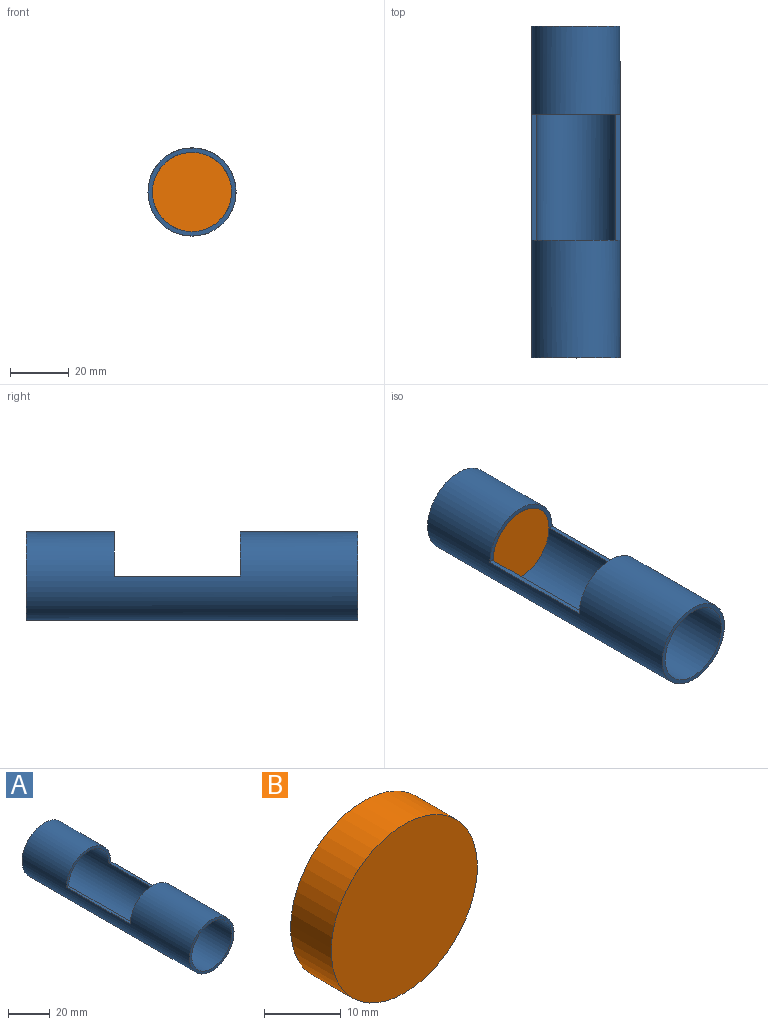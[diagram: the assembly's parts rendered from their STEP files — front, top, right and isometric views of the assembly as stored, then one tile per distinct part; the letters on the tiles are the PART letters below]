
ASSEMBLY  parts=2 mates=1
PART A: 8 faces, bbox 30x113x30 mm
  f0: plane 30x15mm, normal (0,1,0), area 67.2mm2, adj f1,f2,f4,f5
  f1: cylinder r=13.5mm len=113mm, axis (0,1,0), area 7761.3mm2, adj f0,f3,f4,f5,f6,f7
  f2: cylinder r=15mm len=113mm, axis (0,1,0), area 8623.7mm2, adj f0,f3,f4,f5,f6,f7
  f3: plane 30x30mm, normal (0,-1,0), area 134.3mm2, adj f1,f2
  f4: plane 43x1.5mm, normal (0,0,1), area 64.5mm2, adj f0,f1,f2,f6
  f5: plane 43x1.5mm, normal (0,0,1), area 64.5mm2, adj f0,f1,f2,f6
  f6: plane 30x15mm, normal (0,-1,0), area 67.2mm2, adj f1,f2,f4,f5
  f7: plane 30x30mm, normal (0,1,0), area 134.3mm2, adj f1,f2
PART B: 3 faces, bbox 27x7.5x27 mm
  f0: cylinder r=13.5mm len=27mm, axis (0,1,0), area 636.2mm2, adj f1,f2
  f1: plane 27x27mm, normal (0,-1,0), area 572.6mm2, adj f0
  f2: plane 27x27mm, normal (0,1,0), area 572.6mm2, adj f0
PLACE A t=(0.79,-3,19.57)mm
PLACE B t=(0.79,47.5,19.57)mm
MATE fastened B.f0 <-> A.f1  axis (0,-1,0) through (0.79,40,19.57)mm
